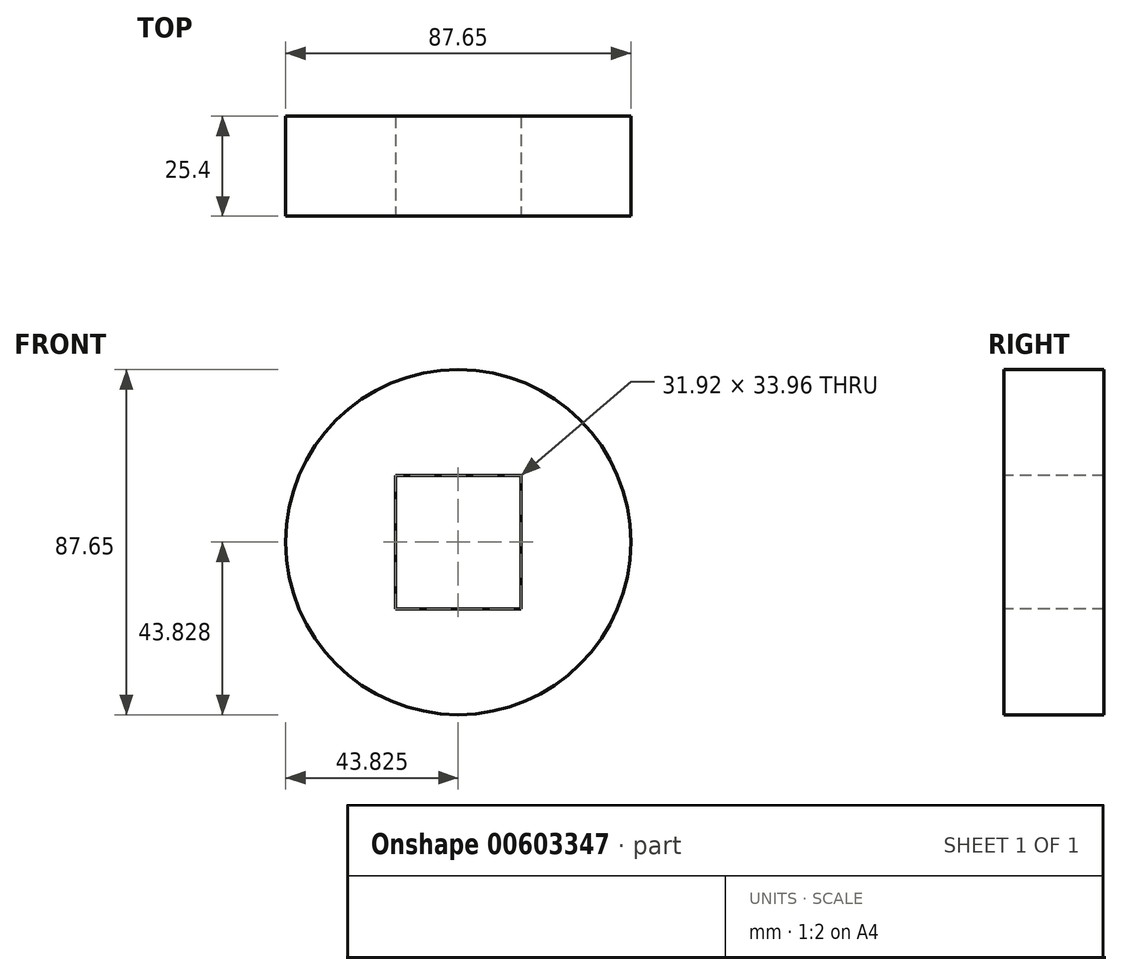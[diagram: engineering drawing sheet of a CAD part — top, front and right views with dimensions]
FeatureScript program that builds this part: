
annotation { "Feature Type Name" : "Feature", "Feature Type Description" : "" }
export const myFeature = defineFeature(function(context is Context, id is Id, definition is map)
    precondition{}
    {
        {
            var Q0;
            Q0=qCreatedBy(makeId("Front.planeOp"),FACE);
            var sketch = newSketch(context, id + "F0", { "sketchPlane" : qUnion([Q0])});
            skCircle(sketch, "E0", {"center": v(-22.3, 20.58) * mm, "radius": 43.83 * mm});
            skSolve(sketch);
        }
        {
            var Q0;
            Q0 = qSketchRegion(id + "F0", true);
            extrude(context, id + "F1", {"entities" : qUnion([Q0]), "depth" : 25.4 * mm, "offsetDistance" : 25.4 * mm});
        }
        {
            var Q0;
            Q0=makeQuery(id+"F1.opExtrude","CAP_FACE",FACE,{"disambiguationData":[OSD([sQuery(id+"F0.wireOp",EDGE,"E0")])],"isStart":false});
            var sketch = newSketch(context, id + "F2", { "sketchPlane" : qUnion([Q0])});
            skLineSegment(sketch, "E1.bottom", {"start": v(-38.27, 3.6) * mm, "end": v(-6.34, 3.6) * mm});
            skLineSegment(sketch, "E1.top", {"start": v(-38.27, 37.56) * mm, "end": v(-6.34, 37.56) * mm});
            skLineSegment(sketch, "E1.left", {"start": v(-38.27, 3.6) * mm, "end": v(-38.27, 37.56) * mm});
            skLineSegment(sketch, "E1.right", {"start": v(-6.34, 3.6) * mm, "end": v(-6.34, 37.56) * mm});
            skPoint(sketch, "E1.middle", {"position": v(-22.3, 20.58) * mm});
            skSolve(sketch);
        }
        {
            var Q0;
            Q0 = qSketchRegion(id + "F2", true);
            extrude(context, id + "F3", {"entities" : qUnion([Q0]), "operationType" : NewBodyOperationType.REMOVE, "oppositeDirection" : true, "depth" : 25.4 * mm, "offsetDistance" : 25.4 * mm});
        }
    });
